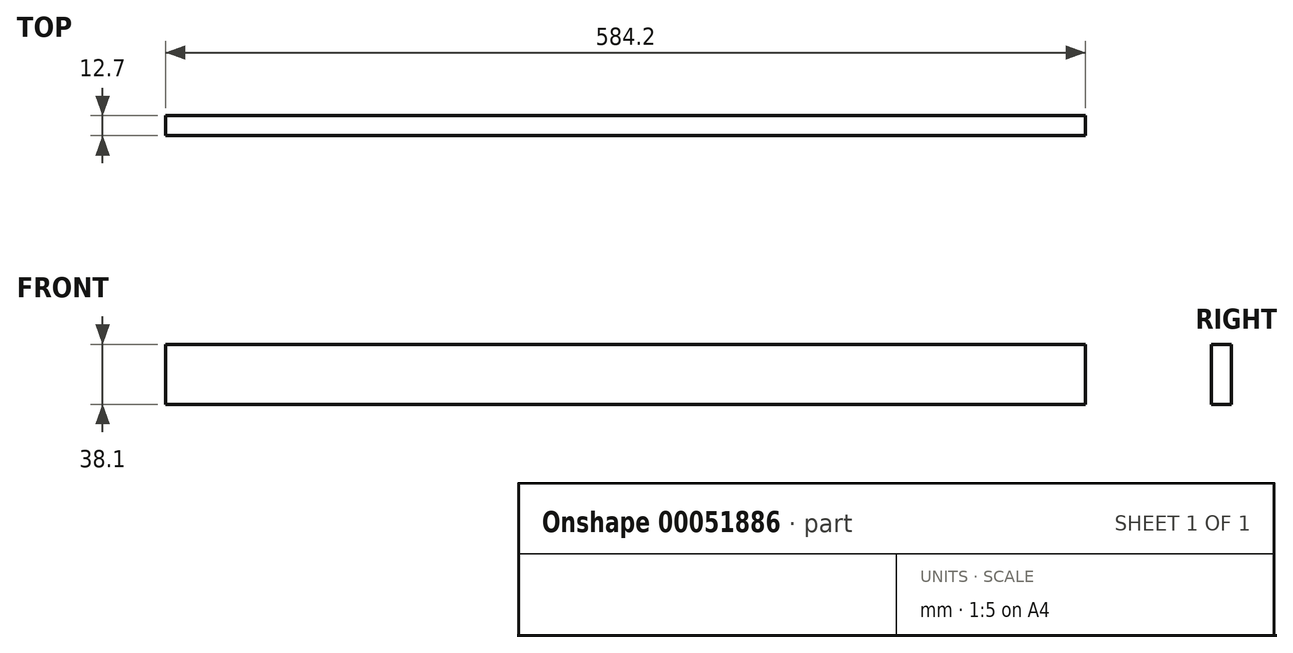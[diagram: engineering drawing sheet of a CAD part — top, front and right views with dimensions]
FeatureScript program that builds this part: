
annotation { "Feature Type Name" : "Feature", "Feature Type Description" : "" }
export const myFeature = defineFeature(function(context is Context, id is Id, definition is map)
    precondition{}
    {
        {
            var Q0;
            Q0=qCreatedBy(makeId("Front.planeOp"),FACE);
            var sketch = newSketch(context, id + "F0", { "sketchPlane" : qUnion([Q0])});
            skLineSegment(sketch, "E0.bottom", {"start": v(-292.1, 0) * mm, "end": v(292.1, 0) * mm});
            skLineSegment(sketch, "E0.top", {"start": v(-292.1, 38.1) * mm, "end": v(292.1, 38.1) * mm});
            skLineSegment(sketch, "E0.left", {"start": v(-292.1, 0) * mm, "end": v(-292.1, 38.1) * mm});
            skLineSegment(sketch, "E0.right", {"start": v(292.1, 0) * mm, "end": v(292.1, 38.1) * mm});
            skSolve(sketch);
        }
        {
            var Q0;
            Q0=makeQuery(id+"F0.imprint","IMPRINT",FACE,{"disambiguationData":[TD([[makeQuery(id+"F0.imprint","IMPRINT",EDGE,{"derivedFrom":sQuery(id+"F0.wireOp",EDGE,"E0.bottom")}),1.0]])]});
            extrude(context, id + "F1", {"entities" : qUnion([Q0]), "depth" : 12.7 * mm});
        }
    });
